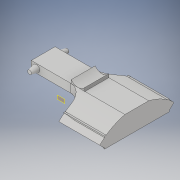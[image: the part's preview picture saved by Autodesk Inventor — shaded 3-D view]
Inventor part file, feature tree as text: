
AUTODESK INVENTOR PART (.ipt)
format: ipt  version: 2018 (Build 220112000, 112)  size: 196,096 bytes
history: native  units: in
note: dims shown in document units (in); Inventor stores cm internally (conversion verified against a paired STEP export)
features: extrude x5, sketch x5, fillet x1, mirror x1, plane x1
ambient origin geometry x8: Origin, YZ Plane, XZ Plane, XY Plane, X Axis, Y Axis, Z Axis, Center Point
bodies: Solid1 (feature_tree)
feature tree (13):
  extrude  "Extrusion1"  Depth=0.2756in
  extrude  "Extrusion2"  Depth=0.0591in
  extrude  "Extrusion3"  Depth=0.0787in
  extrude  "Extrusion4"  TaperAngle=45.0deg  [1 undecoded]
  fillet  "Fillet1"  Radius=0.4724in
  mirror  "Mirror1"
  plane  "Work Plane1"
  extrude  "Extrusion6"  Depth=1.1811in
  sketch  "Sketch1"  dims[d0=1.0827in d1=0.2756in]
  sketch  "Sketch2"  dims[d2=0.0984in d3=0.0in d4=0.0591in]
  sketch  "Sketch3"  dims[d5=0.0787in d6=0.0787in d7=-0.0825in]
  sketch  "Sketch4"  dims[d8=0.5906in d9=45.0deg d10=0.4724in d11=0.0in]
  sketch  "Sketch6"  dims[d12=0.0787in d13=0.1575in d14=0.0394in d15=0.1378in d16=0.0in d17=0.1575in d23=0.2362in d25=0.4724in d26=1.1811in d27=0.748in d28=0.0in]
note: 1 required parameter value undecoded (feature->parameter linkage not recoverable at this tier; creation-order binding heuristic only, values carry confidence <= 0.55)
